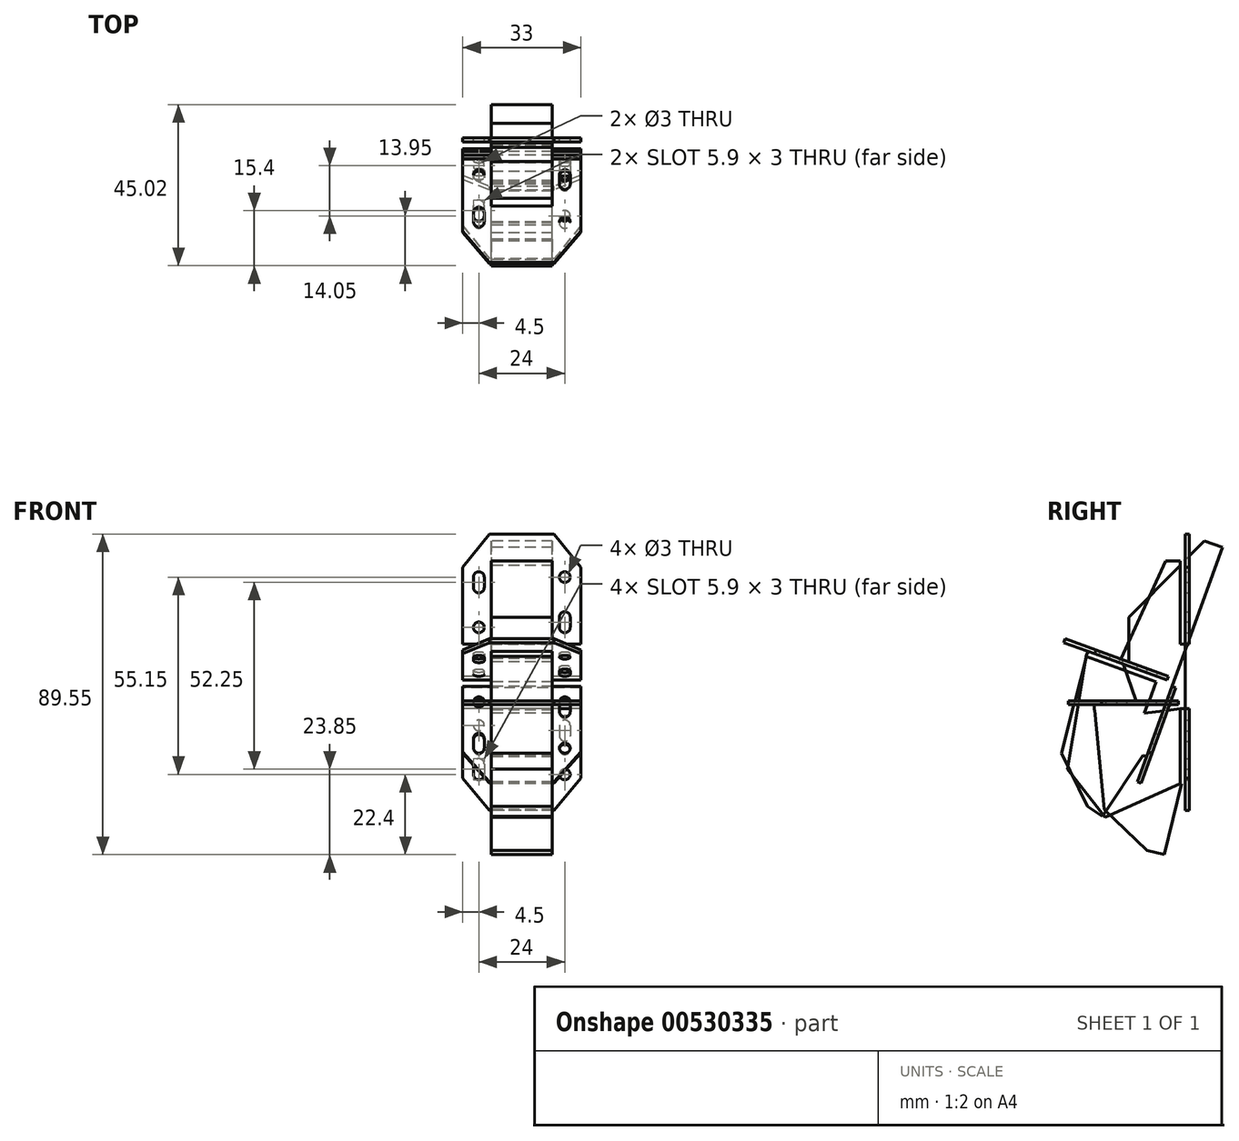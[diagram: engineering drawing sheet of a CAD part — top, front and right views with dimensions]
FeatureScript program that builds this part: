
annotation { "Feature Type Name" : "Feature", "Feature Type Description" : "" }
export const myFeature = defineFeature(function(context is Context, id is Id, definition is map)
    precondition{}
    {
        {
            var Q0;
            Q0=qCreatedBy(makeId("Top.planeOp"),FACE);
            var sketch = newSketch(context, id + "F0", { "sketchPlane" : qUnion([Q0])});
            skLineSegment(sketch, "E0.bottom", {"start": v(16.5, -3) * mm, "end": v(-16.5, -3) * mm});
            skLineSegment(sketch, "E0.top", {"start": v(16.5, -33.75) * mm, "end": v(-16.5, -33.75) * mm, "construction": true});
            skLineSegment(sketch, "E0.left", {"start": v(16.5, -3) * mm, "end": v(16.5, -33.75) * mm, "construction": true});
            skLineSegment(sketch, "E0.right", {"start": v(-16.5, -3) * mm, "end": v(-16.5, -33.75) * mm, "construction": true});
            skPoint(sketch, "E0.middle", {"position": v(0, -18.38) * mm});
            skLineSegment(sketch, "E1", {"start": v(-16.5, -3) * mm, "end": v(-16.5, -24.5) * mm});
            skLineSegment(sketch, "E2", {"start": v(-16.5, -24.5) * mm, "end": v(-9, -33.75) * mm});
            skLineSegment(sketch, "E3", {"start": v(0, -3) * mm, "end": v(0, -33.75) * mm, "construction": true});
            skLineSegment(sketch, "E4.MirrorCS", {"start": v(16.5, -24.5) * mm, "end": v(9, -33.75) * mm});
            skLineSegment(sketch, "E5", {"start": v(16.5, -24.5) * mm, "end": v(16.5, -3) * mm});
            skLineSegment(sketch, "E6", {"start": v(9, -33.75) * mm, "end": v(-9, -33.75) * mm});
            skCircle(sketch, "E7", {"center": v(-12, -7.7) * mm, "radius": 1.5 * mm});
            skLineSegment(sketch, "E8", {"start": v(-12, -21.75) * mm, "end": v(-12, -18.85) * mm, "construction": true});
            skLineSegment(sketch, "E9", {"start": v(-12, -7.7) * mm, "end": v(12, -21.75) * mm, "construction": true});
            skPoint(sketch, "E10", {"position": v(0, -14.72) * mm});
            skCircle(sketch, "E11", {"center": v(12, -21.75) * mm, "radius": 1.5 * mm});
            skLineSegment(sketch, "E12", {"start": v(12, -7.7) * mm, "end": v(12, -10.6) * mm, "construction": true});
            skArc(sketch, "E13.0.startCap", {"start": v(10.5, -7.7) * mm, "mid": v(12, -6.2) * mm, "end": v(13.5, -7.7) * mm});
            skArc(sketch, "E13.0.endCap", {"start": v(13.5, -10.6) * mm, "mid": v(12, -12.1) * mm, "end": v(10.5, -10.6) * mm});
            skLineSegment(sketch, "E13.0.left", {"start": v(13.5, -7.7) * mm, "end": v(13.5, -10.6) * mm});
            skLineSegment(sketch, "E13.0.right", {"start": v(10.5, -7.7) * mm, "end": v(10.5, -10.6) * mm});
            skArc(sketch, "E13.1.startCap", {"start": v(-10.5, -21.75) * mm, "mid": v(-12, -23.25) * mm, "end": v(-13.5, -21.75) * mm});
            skArc(sketch, "E13.1.endCap", {"start": v(-13.5, -18.85) * mm, "mid": v(-12, -17.35) * mm, "end": v(-10.5, -18.85) * mm});
            skLineSegment(sketch, "E13.1.left", {"start": v(-13.5, -21.75) * mm, "end": v(-13.5, -18.85) * mm});
            skLineSegment(sketch, "E13.1.right", {"start": v(-10.5, -21.75) * mm, "end": v(-10.5, -18.85) * mm});
            skLineSegment(sketch, "E14", {"start": v(-16.5, 0) * mm, "end": v(16.5, 0) * mm, "construction": true});
            skSolve(sketch);
        }
        {
            var Q0;
            Q0 = qSketchRegion(id + "F0", true);
            extrude(context, id + "F1", {"entities" : qUnion([Q0]), "oppositeDirection" : true, "depth" : 1.1 * mm, "offsetDistance" : 25 * mm});
        }
        {
            var Q0;
            Q0=qCreatedBy(makeId("Front.planeOp"),FACE);
            var sketch = newSketch(context, id + "F2", { "sketchPlane" : qUnion([Q0])});
            skLineSegment(sketch, "E15.bottom", {"start": v(16.5, -2.2) * mm, "end": v(-16.5, -2.2) * mm});
            skLineSegment(sketch, "E15.top", {"start": v(16.5, -30.7) * mm, "end": v(-16.5, -30.7) * mm, "construction": true});
            skLineSegment(sketch, "E15.left", {"start": v(16.5, -2.2) * mm, "end": v(16.5, -30.7) * mm, "construction": true});
            skLineSegment(sketch, "E15.right", {"start": v(-16.5, -2.2) * mm, "end": v(-16.5, -30.7) * mm, "construction": true});
            skPoint(sketch, "E15.middle", {"position": v(0, -16.45) * mm});
            skLineSegment(sketch, "E16", {"start": v(-16.5, -21.7) * mm, "end": v(-9, -30.7) * mm});
            skLineSegment(sketch, "E17", {"start": v(0, -2.2) * mm, "end": v(0, -30.7) * mm, "construction": true});
            skLineSegment(sketch, "E18.MirrorCS", {"start": v(16.5, -21.7) * mm, "end": v(9, -30.7) * mm});
            skLineSegment(sketch, "E19", {"start": v(9, -30.7) * mm, "end": v(-9, -30.7) * mm});
            skLineSegment(sketch, "E20", {"start": v(-16.5, -2.2) * mm, "end": v(-16.5, -21.7) * mm});
            skLineSegment(sketch, "E21", {"start": v(16.5, -2.2) * mm, "end": v(16.5, -21.7) * mm});
            skLineSegment(sketch, "E22", {"start": v(-12, -17.7) * mm, "end": v(-12, -20.6) * mm, "construction": true});
            skLineSegment(sketch, "E23", {"start": v(12, -6.9) * mm, "end": v(12, -9.8) * mm, "construction": true});
            skCircle(sketch, "E24", {"center": v(-12, -6.9) * mm, "radius": 1.5 * mm});
            skCircle(sketch, "E25", {"center": v(12, -20.6) * mm, "radius": 1.5 * mm});
            skArc(sketch, "E26.0.startCap", {"start": v(-13.5, -17.7) * mm, "mid": v(-12, -16.2) * mm, "end": v(-10.5, -17.7) * mm});
            skArc(sketch, "E26.0.endCap", {"start": v(-10.5, -20.6) * mm, "mid": v(-12, -22.1) * mm, "end": v(-13.5, -20.6) * mm});
            skLineSegment(sketch, "E26.0.left", {"start": v(-10.5, -17.7) * mm, "end": v(-10.5, -20.6) * mm});
            skLineSegment(sketch, "E26.0.right", {"start": v(-13.5, -17.7) * mm, "end": v(-13.5, -20.6) * mm});
            skArc(sketch, "E26.1.startCap", {"start": v(10.5, -6.9) * mm, "mid": v(12, -5.4) * mm, "end": v(13.5, -6.9) * mm});
            skArc(sketch, "E26.1.endCap", {"start": v(13.5, -9.8) * mm, "mid": v(12, -11.3) * mm, "end": v(10.5, -9.8) * mm});
            skLineSegment(sketch, "E26.1.left", {"start": v(13.5, -6.9) * mm, "end": v(13.5, -9.8) * mm});
            skLineSegment(sketch, "E26.1.right", {"start": v(10.5, -6.9) * mm, "end": v(10.5, -9.8) * mm});
            skSolve(sketch);
        }
        {
            var Q0;
            Q0 = qSketchRegion(id + "F2", true);
            extrude(context, id + "F3", {"entities" : qUnion([Q0]), "depth" : 1.1 * mm, "offsetDistance" : 25 * mm});
        }
        {
            var Q0;
            Q0=qCreatedBy(makeId("Right.planeOp"),FACE);
            var sketch = newSketch(context, id + "F4", { "sketchPlane" : qUnion([Q0])});
            skLineSegment(sketch, "E27", {"start": v(-1.1, -0.7) * mm, "end": v(-26.5, -0.7) * mm});
            skLineSegment(sketch, "E28", {"start": v(-26.5, -0.7) * mm, "end": v(-26.5, -1.9) * mm});
            skLineSegment(sketch, "E29", {"start": v(-26.5, -1.9) * mm, "end": v(-23.75, -30.37) * mm});
            skLineSegment(sketch, "E30", {"start": v(-23.75, -30.37) * mm, "end": v(-11.85, -41.8) * mm});
            skLineSegment(sketch, "E31", {"start": v(-11.85, -41.8) * mm, "end": v(-7, -43) * mm});
            skLineSegment(sketch, "E32", {"start": v(-7, -43) * mm, "end": v(-2.1, -23.2) * mm});
            skLineSegment(sketch, "E33", {"start": v(-2.1, -23.2) * mm, "end": v(-1.1, -23.2) * mm});
            skLineSegment(sketch, "E34", {"start": v(-1.1, -23.2) * mm, "end": v(-1.1, -0.7) * mm});
            skSolve(sketch);
        }
        {
            var Q0;
            Q0 = qSketchRegion(id + "F4", true);
            extrude(context, id + "F5", {"entities" : qUnion([Q0]), "endBound" : BoundingType.SYMMETRIC, "depth" : 17 * mm, "offsetDistance" : 25 * mm});
        }
        {
            var Q0;
            Q0=makeQuery(id+"F1.opExtrude","SWEPT_BODY",BODY,{"disambiguationData":[OSD([sQuery(id+"F0.wireOp",EDGE,"E0.bottom"),sQuery(id+"F0.wireOp",EDGE,"E1"),sQuery(id+"F0.wireOp",EDGE,"E2"),sQuery(id+"F0.wireOp",EDGE,"E4.MirrorCS"),sQuery(id+"F0.wireOp",EDGE,"E5"),sQuery(id+"F0.wireOp",EDGE,"E6"),sQuery(id+"F0.wireOp",EDGE,"E7"),sQuery(id+"F0.wireOp",EDGE,"E11"),sQuery(id+"F0.wireOp",EDGE,"E13.0.startCap"),sQuery(id+"F0.wireOp",EDGE,"E13.0.endCap"),sQuery(id+"F0.wireOp",EDGE,"E13.0.left"),sQuery(id+"F0.wireOp",EDGE,"E13.0.right"),sQuery(id+"F0.wireOp",EDGE,"E13.1.startCap"),sQuery(id+"F0.wireOp",EDGE,"E13.1.endCap"),sQuery(id+"F0.wireOp",EDGE,"E13.1.left"),sQuery(id+"F0.wireOp",EDGE,"E13.1.right")])]});
            var Q1;
            Q1=sQuery(id+"F0.wireOp",EDGE,"E14");
            transform(context, id + "F6", {"entities" : qUnion([Q0]), "transformType" : TransformType.ROTATION, "transformAxis" : qUnion([Q1]), "angle" : 90 * degree, "oppositeDirection" : true, "makeCopy" : true});
        }
        {
            var Q0;
            Q0=makeQuery(id+"F6.opPattern","COPY",BODY,{"derivedFrom":makeQuery(id+"F1.opExtrude","SWEPT_BODY",BODY,{"disambiguationData":[OSD([sQuery(id+"F0.wireOp",EDGE,"E0.bottom"),sQuery(id+"F0.wireOp",EDGE,"E1"),sQuery(id+"F0.wireOp",EDGE,"E2"),sQuery(id+"F0.wireOp",EDGE,"E4.MirrorCS"),sQuery(id+"F0.wireOp",EDGE,"E5"),sQuery(id+"F0.wireOp",EDGE,"E6"),sQuery(id+"F0.wireOp",EDGE,"E7"),sQuery(id+"F0.wireOp",EDGE,"E11"),sQuery(id+"F0.wireOp",EDGE,"E13.0.startCap"),sQuery(id+"F0.wireOp",EDGE,"E13.0.endCap"),sQuery(id+"F0.wireOp",EDGE,"E13.0.left"),sQuery(id+"F0.wireOp",EDGE,"E13.0.right"),sQuery(id+"F0.wireOp",EDGE,"E13.1.startCap"),sQuery(id+"F0.wireOp",EDGE,"E13.1.endCap"),sQuery(id+"F0.wireOp",EDGE,"E13.1.left"),sQuery(id+"F0.wireOp",EDGE,"E13.1.right")])]}),"instanceName":"1"});
            transform(context, id + "F7", {"entities" : qUnion([Q0]), "transformType" : TransformType.TRANSLATION_3D, "dx" : 0 * mm, "dy" : 0 * mm, "dz" : (18 - 5.2) * mm, "makeCopy" : false});
        }
        {
            var Q0;
            Q0=qCreatedBy(makeId("Right.planeOp"),FACE);
            var sketch = newSketch(context, id + "F8", { "sketchPlane" : qUnion([Q0])});
            skLineSegment(sketch, "E35", {"start": v(-1.1, 39.05) * mm, "end": v(-6.6, 39.05) * mm});
            skLineSegment(sketch, "E36", {"start": v(-6.6, 39.05) * mm, "end": v(-19, 11.73) * mm});
            skLineSegment(sketch, "E37", {"start": v(-19, 11.73) * mm, "end": v(-6.6, -23.2) * mm});
            skLineSegment(sketch, "E38", {"start": v(-6.6, -23.2) * mm, "end": v(-1.1, -23.2) * mm});
            skLineSegment(sketch, "E39", {"start": v(-1.1, -23.2) * mm, "end": v(-1.1, 39.05) * mm});
            skSolve(sketch);
        }
        {
            var Q0;
            Q0 = qSketchRegion(id + "F8", true);
            extrude(context, id + "F9", {"entities" : qUnion([Q0]), "endBound" : BoundingType.SYMMETRIC, "depth" : 17 * mm, "offsetDistance" : 25 * mm});
        }
        {
            var Q0;
            Q0=makeQuery(id+"F3.opExtrude","CAP_FACE",FACE,{"disambiguationData":[OSD([sQuery(id+"F2.wireOp",EDGE,"E15.bottom"),sQuery(id+"F2.wireOp",EDGE,"E16"),sQuery(id+"F2.wireOp",EDGE,"E18.MirrorCS"),sQuery(id+"F2.wireOp",EDGE,"E19"),sQuery(id+"F2.wireOp",EDGE,"E20"),sQuery(id+"F2.wireOp",EDGE,"E21"),sQuery(id+"F2.wireOp",EDGE,"E24"),sQuery(id+"F2.wireOp",EDGE,"E25"),sQuery(id+"F2.wireOp",EDGE,"E26.0.startCap"),sQuery(id+"F2.wireOp",EDGE,"E26.0.endCap"),sQuery(id+"F2.wireOp",EDGE,"E26.0.left"),sQuery(id+"F2.wireOp",EDGE,"E26.0.right"),sQuery(id+"F2.wireOp",EDGE,"E26.1.startCap"),sQuery(id+"F2.wireOp",EDGE,"E26.1.endCap"),sQuery(id+"F2.wireOp",EDGE,"E26.1.left"),sQuery(id+"F2.wireOp",EDGE,"E26.1.right")])],"isStart":false});
            var sketch = newSketch(context, id + "F10", { "sketchPlane" : qUnion([Q0])});
            skLineSegment(sketch, "E40.bottom", {"start": v(8.5, -2.2) * mm, "end": v(-8.5, -2.2) * mm});
            skLineSegment(sketch, "E40.top", {"start": v(8.5, -23.2) * mm, "end": v(-8.5, -23.2) * mm});
            skLineSegment(sketch, "E40.left", {"start": v(8.5, -2.2) * mm, "end": v(8.5, -23.2) * mm});
            skLineSegment(sketch, "E40.right", {"start": v(-8.5, -2.2) * mm, "end": v(-8.5, -23.2) * mm});
            skSolve(sketch);
        }
        {
            var Q0;
            Q0 = qSketchRegion(id + "F10", true);
            extrude(context, id + "F11", {"entities" : qUnion([Q0]), "operationType" : NewBodyOperationType.ADD, "depth" : 1.5 * mm, "offsetDistance" : 25 * mm});
        }
        {
            var Q0;
            Q0=makeQuery(id+"F1.opExtrude","CAP_FACE",FACE,{"disambiguationData":[OSD([sQuery(id+"F0.wireOp",EDGE,"E0.bottom"),sQuery(id+"F0.wireOp",EDGE,"E1"),sQuery(id+"F0.wireOp",EDGE,"E2"),sQuery(id+"F0.wireOp",EDGE,"E4.MirrorCS"),sQuery(id+"F0.wireOp",EDGE,"E5"),sQuery(id+"F0.wireOp",EDGE,"E6"),sQuery(id+"F0.wireOp",EDGE,"E7"),sQuery(id+"F0.wireOp",EDGE,"E11"),sQuery(id+"F0.wireOp",EDGE,"E13.0.startCap"),sQuery(id+"F0.wireOp",EDGE,"E13.0.endCap"),sQuery(id+"F0.wireOp",EDGE,"E13.0.left"),sQuery(id+"F0.wireOp",EDGE,"E13.0.right"),sQuery(id+"F0.wireOp",EDGE,"E13.1.startCap"),sQuery(id+"F0.wireOp",EDGE,"E13.1.endCap"),sQuery(id+"F0.wireOp",EDGE,"E13.1.left"),sQuery(id+"F0.wireOp",EDGE,"E13.1.right")])],"isStart":false});
            var sketch = newSketch(context, id + "F12", { "sketchPlane" : qUnion([Q0])});
            skLineSegment(sketch, "E41.bottom", {"start": v(8.5, 26.5) * mm, "end": v(-8.5, 26.5) * mm});
            skLineSegment(sketch, "E41.top", {"start": v(8.5, 3) * mm, "end": v(-8.5, 3) * mm});
            skLineSegment(sketch, "E41.left", {"start": v(8.5, 26.5) * mm, "end": v(8.5, 3) * mm});
            skLineSegment(sketch, "E41.right", {"start": v(-8.5, 26.5) * mm, "end": v(-8.5, 3) * mm});
            skSolve(sketch);
        }
        {
            var Q0;
            Q0 = qSketchRegion(id + "F12", true);
            extrude(context, id + "F13", {"entities" : qUnion([Q0]), "operationType" : NewBodyOperationType.ADD, "depth" : 1.5 * mm, "offsetDistance" : 25 * mm});
        }
        {
            var Q0;
            Q0=makeQuery(id+"F1.opExtrude","SWEPT_BODY",BODY,{"disambiguationData":[OSD([sQuery(id+"F0.wireOp",EDGE,"E0.bottom"),sQuery(id+"F0.wireOp",EDGE,"E1"),sQuery(id+"F0.wireOp",EDGE,"E2"),sQuery(id+"F0.wireOp",EDGE,"E4.MirrorCS"),sQuery(id+"F0.wireOp",EDGE,"E5"),sQuery(id+"F0.wireOp",EDGE,"E6"),sQuery(id+"F0.wireOp",EDGE,"E7"),sQuery(id+"F0.wireOp",EDGE,"E11"),sQuery(id+"F0.wireOp",EDGE,"E13.0.startCap"),sQuery(id+"F0.wireOp",EDGE,"E13.0.endCap"),sQuery(id+"F0.wireOp",EDGE,"E13.0.left"),sQuery(id+"F0.wireOp",EDGE,"E13.0.right"),sQuery(id+"F0.wireOp",EDGE,"E13.1.startCap"),sQuery(id+"F0.wireOp",EDGE,"E13.1.endCap"),sQuery(id+"F0.wireOp",EDGE,"E13.1.left"),sQuery(id+"F0.wireOp",EDGE,"E13.1.right")])]});
            var Q1;
            Q1=sQuery(id+"F0.wireOp",EDGE,"E14");
            var Q2;
            Q2=sQuery(id+"F0.wireOp",EDGE,"E14");
            transform(context, id + "F14", {"entities" : qUnion([Q0]), "transformType" : TransformType.ROTATION, "transformAxis" : qUnion([Q2]), "angle" : 20 * degree, "oppositeDirection" : true, "makeCopy" : true});
        }
        {
            var Q0;
            Q0=makeQuery(id+"F14.opPattern","COPY",BODY,{"derivedFrom":makeQuery(id+"F1.opExtrude","SWEPT_BODY",BODY,{"disambiguationData":[OSD([sQuery(id+"F0.wireOp",EDGE,"E0.bottom"),sQuery(id+"F0.wireOp",EDGE,"E1"),sQuery(id+"F0.wireOp",EDGE,"E2"),sQuery(id+"F0.wireOp",EDGE,"E4.MirrorCS"),sQuery(id+"F0.wireOp",EDGE,"E5"),sQuery(id+"F0.wireOp",EDGE,"E6"),sQuery(id+"F0.wireOp",EDGE,"E7"),sQuery(id+"F0.wireOp",EDGE,"E11"),sQuery(id+"F0.wireOp",EDGE,"E13.0.startCap"),sQuery(id+"F0.wireOp",EDGE,"E13.0.endCap"),sQuery(id+"F0.wireOp",EDGE,"E13.0.left"),sQuery(id+"F0.wireOp",EDGE,"E13.0.right"),sQuery(id+"F0.wireOp",EDGE,"E13.1.startCap"),sQuery(id+"F0.wireOp",EDGE,"E13.1.endCap"),sQuery(id+"F0.wireOp",EDGE,"E13.1.left"),sQuery(id+"F0.wireOp",EDGE,"E13.1.right")])]}),"instanceName":"1"});
            transform(context, id + "F15", {"entities" : qUnion([Q0]), "transformType" : TransformType.TRANSLATION_3D, "dx" : 0 * mm, "dy" : -3 * mm, "dz" : 5.75 * mm, "makeCopy" : false});
        }
        {
            var Q0;
            Q0=qCreatedBy(makeId("Right.planeOp"),FACE);
            var sketch = newSketch(context, id + "F16", { "sketchPlane" : qUnion([Q0])});
            skLineSegment(sketch, "E42", {"start": v(-28.8, 12.37) * mm, "end": v(-34, -19.15) * mm});
            skLineSegment(sketch, "E43.0", {"start": v(-28.8, 12.37) * mm, "end": v(-9.31, 5.28) * mm});
            skLineSegment(sketch, "E44", {"start": v(-34, -19.15) * mm, "end": v(-23.5, -32.55) * mm});
            skLineSegment(sketch, "E45", {"start": v(-23.5, -32.55) * mm, "end": v(-2.6, -23.2) * mm});
            skLineSegment(sketch, "E46.0", {"start": v(-2.6, -2.2) * mm, "end": v(-2.6, -23.2) * mm});
            skLineSegment(sketch, "E47", {"start": v(-2.6, -2.2) * mm, "end": v(-12.51, -3.51) * mm});
            skLineSegment(sketch, "E48", {"start": v(-12.51, -3.51) * mm, "end": v(-9.31, 5.28) * mm});
            skPoint(sketch, "E49.orphan", {"position": v(-6.7, 4.33) * mm});
            skSolve(sketch);
        }
        {
            var Q0;
            Q0 = qSketchRegion(id + "F16", true);
            var Q1;
            Q1=makeQuery(id+"F14.opPattern","COPY",VERTEX,{"derivedFrom":makeQuery(id+"F13.opExtrude","CAP_VERTEX",VERTEX,{"disambiguationData":[OSD([sQuery(id+"F12.wireOp",EDGE,"E41.bottom"),sQuery(id+"F12.wireOp",EDGE,"E41.left")])],"isStart":false}),"instanceName":"1"});
            var Q2;
            Q2=makeQuery(id+"F14.opPattern","COPY",VERTEX,{"derivedFrom":makeQuery(id+"F13.opExtrude","CAP_VERTEX",VERTEX,{"disambiguationData":[OSD([sQuery(id+"F12.wireOp",EDGE,"E41.bottom"),sQuery(id+"F12.wireOp",EDGE,"E41.right")])],"isStart":false}),"instanceName":"1"});
            extrude(context, id + "F17", {"entities" : qUnion([Q0]), "endBound" : BoundingType.UP_TO_VERTEX, "depth" : 25 * mm, "endBoundEntityVertex" : qUnion([Q1]), "offsetDistance" : 25 * mm, "hasSecondDirection" : true, "secondDirectionBound" : SecondDirectionBoundingType.UP_TO_VERTEX, "secondDirectionOppositeDirection" : true, "secondDirectionDepth" : 25 * mm, "secondDirectionBoundEntityVertex" : qUnion([Q2])});
        }
        {
            var Q0;
            Q0=makeQuery(id+"F9.opExtrude","CAP_FACE",FACE,{"disambiguationData":[OSD([sQuery(id+"F8.wireOp",EDGE,"E35"),sQuery(id+"F8.wireOp",EDGE,"E36"),sQuery(id+"F8.wireOp",EDGE,"E37"),sQuery(id+"F8.wireOp",EDGE,"E38"),sQuery(id+"F8.wireOp",EDGE,"E39")])],"isStart":false});
            var sketch = newSketch(context, id + "F18", { "sketchPlane" : qUnion([Q0])});
            skLineSegment(sketch, "E50.bottom", {"start": v(-1.1, 39.05) * mm, "end": v(-2.6, 39.05) * mm});
            skLineSegment(sketch, "E50.top", {"start": v(-1.1, 15.8) * mm, "end": v(-2.6, 15.8) * mm});
            skLineSegment(sketch, "E50.left", {"start": v(-1.1, 39.05) * mm, "end": v(-1.1, 15.8) * mm});
            skLineSegment(sketch, "E50.right", {"start": v(-2.6, 39.05) * mm, "end": v(-2.6, 15.8) * mm});
            skLineSegment(sketch, "E51.bottom", {"start": v(-2.6, -23.2) * mm, "end": v(-1.1, -23.2) * mm});
            skLineSegment(sketch, "E51.top", {"start": v(-2.6, -2.2) * mm, "end": v(-1.1, -2.2) * mm});
            skLineSegment(sketch, "E51.left", {"start": v(-2.6, -23.2) * mm, "end": v(-2.6, -2.2) * mm});
            skLineSegment(sketch, "E51.right", {"start": v(-1.1, -23.2) * mm, "end": v(-1.1, -2.2) * mm});
            skSolve(sketch);
        }
        {
            var Q0;
            Q0 = qSketchRegion(id + "F18", true);
            extrude(context, id + "F19", {"entities" : qUnion([Q0]), "operationType" : NewBodyOperationType.REMOVE, "endBound" : BoundingType.THROUGH_ALL, "oppositeDirection" : true, "depth" : 25 * mm, "offsetDistance" : 25 * mm});
        }
    });
